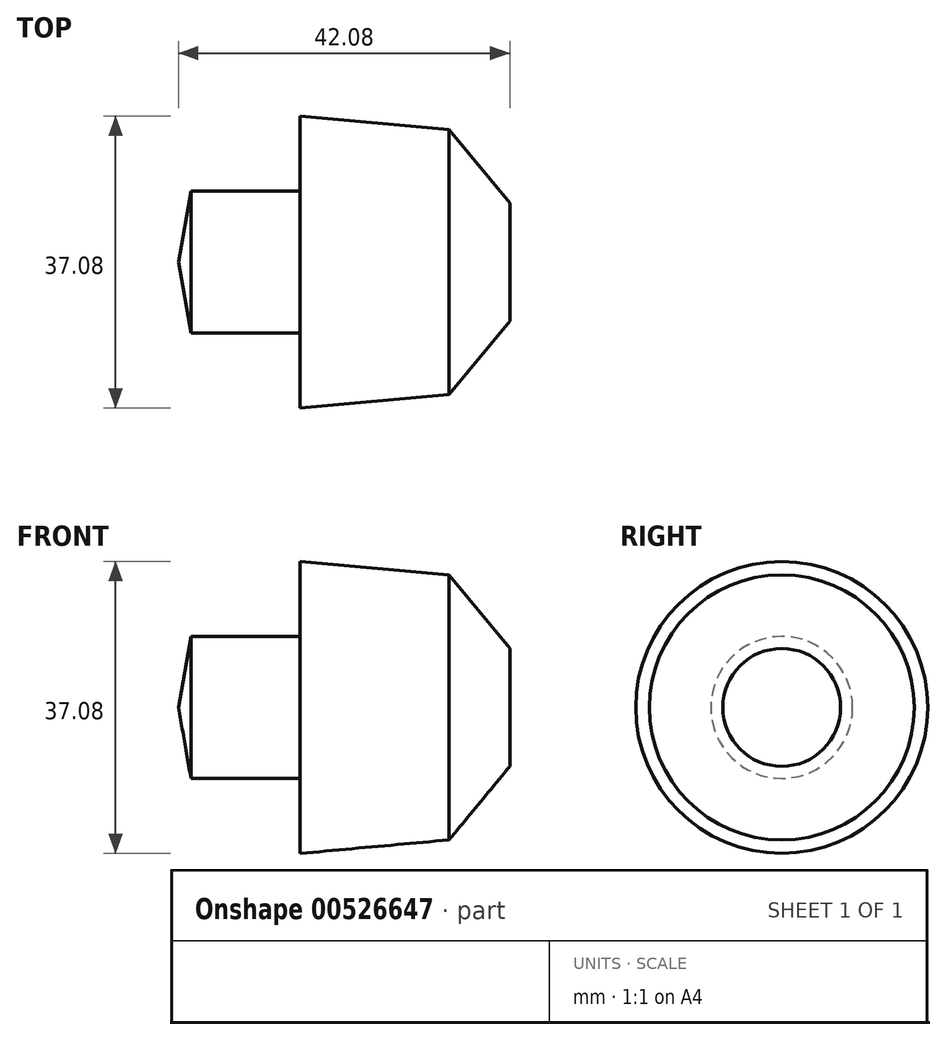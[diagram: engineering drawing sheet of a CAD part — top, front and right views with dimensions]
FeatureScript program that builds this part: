
annotation { "Feature Type Name" : "Feature", "Feature Type Description" : "" }
export const myFeature = defineFeature(function(context is Context, id is Id, definition is map)
    precondition{}
    {
        {
            var Q0;
            Q0=qCreatedBy(makeId("Front.planeOp"),FACE);
            var sketch = newSketch(context, id + "F0", { "sketchPlane" : qUnion([Q0])});
            skLineSegment(sketch, "E0", {"start": v(0, 0) * mm, "end": v(1.57, 9) * mm});
            skLineSegment(sketch, "E1", {"start": v(1.57, 9) * mm, "end": v(15.46, 9) * mm});
            skLineSegment(sketch, "E2", {"start": v(15.46, 9) * mm, "end": v(15.46, 18.54) * mm});
            skLineSegment(sketch, "E3", {"start": v(15.46, 18.54) * mm, "end": v(34.36, 16.82) * mm});
            skLineSegment(sketch, "E4", {"start": v(34.36, 16.82) * mm, "end": v(42.08, 7.48) * mm});
            skLineSegment(sketch, "E5", {"start": v(42.08, 7.48) * mm, "end": v(42.08, 0) * mm});
            skLineSegment(sketch, "E6", {"start": v(42.08, 0) * mm, "end": v(0, 0) * mm});
            skSolve(sketch);
        }
        {
            var Q0;
            Q0=makeQuery(id+"F0.imprint","IMPRINT",FACE,{"disambiguationData":[TD([[makeQuery(id+"F0.imprint","IMPRINT",EDGE,{"derivedFrom":sQuery(id+"F0.wireOp",EDGE,"E0")}),-1.0]])]});
            var Q1;
            Q1=sQuery(id+"F0.wireOp",EDGE,"E6");
            revolve(context, id + "F1", {"entities" : qUnion([Q0]), "axis" : qUnion([Q1]), "revolveType" : RevolveType.FULL});
        }
    });
